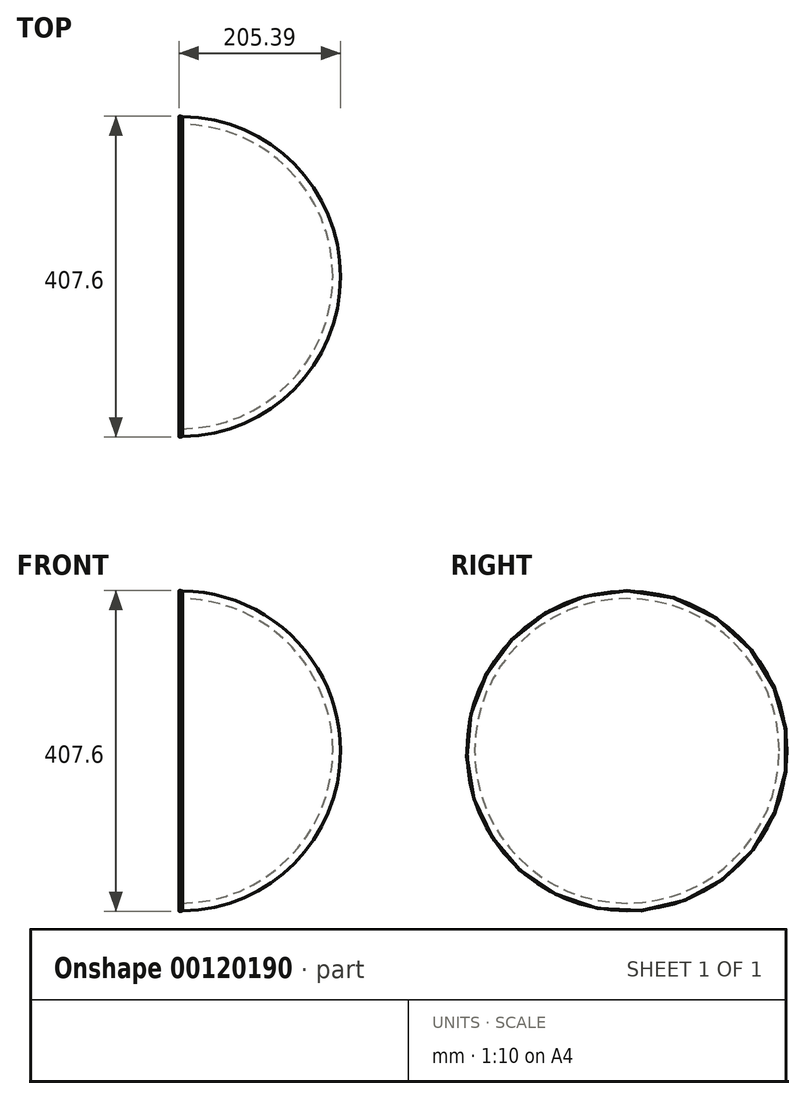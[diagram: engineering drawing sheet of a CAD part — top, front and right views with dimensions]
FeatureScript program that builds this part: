
annotation { "Feature Type Name" : "Feature", "Feature Type Description" : "" }
export const myFeature = defineFeature(function(context is Context, id is Id, definition is map)
    precondition{}
    {
        {
            var Q0;
            Q0=qCreatedBy(makeId("Front.planeOp"),FACE);
            var sketch = newSketch(context, id + "F0", { "sketchPlane" : qUnion([Q0])});
            skLineSegment(sketch, "E0", {"start": v(-38.96, 0) * mm, "end": v(64.2, 0) * mm});
            skArc(sketch, "E1", {"start": v(203.2, 0) * mm, "mid": v(143.68, 143.68) * mm, "end": v(0, 203.2) * mm});
            skArc(sketch, "E2", {"start": v(0, 193.4) * mm, "mid": v(136.75, 136.75) * mm, "end": v(193.4, 0) * mm});
            skArc(sketch, "E3", {"start": v(0, 203.2) * mm, "mid": v(143.68, 143.68) * mm, "end": v(203.2, 0) * mm});
            skLineSegment(sketch, "E4", {"start": v(203.2, 0) * mm, "end": v(193.4, 0) * mm});
            skLineSegment(sketch, "E5", {"start": v(0, 193.4) * mm, "end": v(0, 203.2) * mm});
            skSolve(sketch);
        }
        {
            var Q0;
            Q0 = qSketchRegion(id + "F0", true);
            var Q1;
            Q1=sQuery(id+"F0.wireOp",EDGE,"E0");
            revolve(context, id + "F1", {"entities" : qUnion([Q0]), "axis" : qUnion([Q1]), "revolveType" : RevolveType.FULL});
        }
        {
            var Q0;
            Q0=qCreatedBy(makeId("Front.planeOp"),FACE);
            var sketch = newSketch(context, id + "F2", { "sketchPlane" : qUnion([Q0])});
            skFitSpline(sketch, "E6", {"points": [v(0, 203.3) * mm, v(0, 203.2) * mm, v(1.15, 203.14) * mm, v(2.1, 203.06) * mm, v(2.34, 203.09) * mm, v(2.14, 203.38) * mm, v(1.71, 203.36) * mm, v(1.36, 203.5) * mm, v(0.96, 203.52) * mm, v(0.62, 203.65) * mm, v(0.37, 203.6) * mm, v(0, 203.78) * mm, v(-0.35, 203.74) * mm, v(-0.5, 203.63) * mm, v(-0.85, 203.68) * mm, v(-1.17, 203.73) * mm, v(-1.65, 203.65) * mm, v(-1.97, 203.52) * mm, v(-2.15, 203.52) * mm, v(-2.18, 203.38) * mm, v(-1.99, 203.26) * mm, v(-1.62, 203.25) * mm, v(-1.14, 203.15) * mm, v(-0.83, 203.25) * mm, v(-0.58, 203.2) * mm, v(-0.4, 203.15) * mm, v(0, 203.3) * mm]});
            skSolve(sketch);
        }
        {
            var Q0;
            Q0 = qSketchRegion(id + "F2", true);
            var Q1;
            Q1=sQuery(id+"F0.wireOp",EDGE,"E0");
            revolve(context, id + "F3", {"operationType" : NewBodyOperationType.ADD, "entities" : qUnion([Q0]), "axis" : qUnion([Q1]), "revolveType" : RevolveType.FULL});
        }
    });
